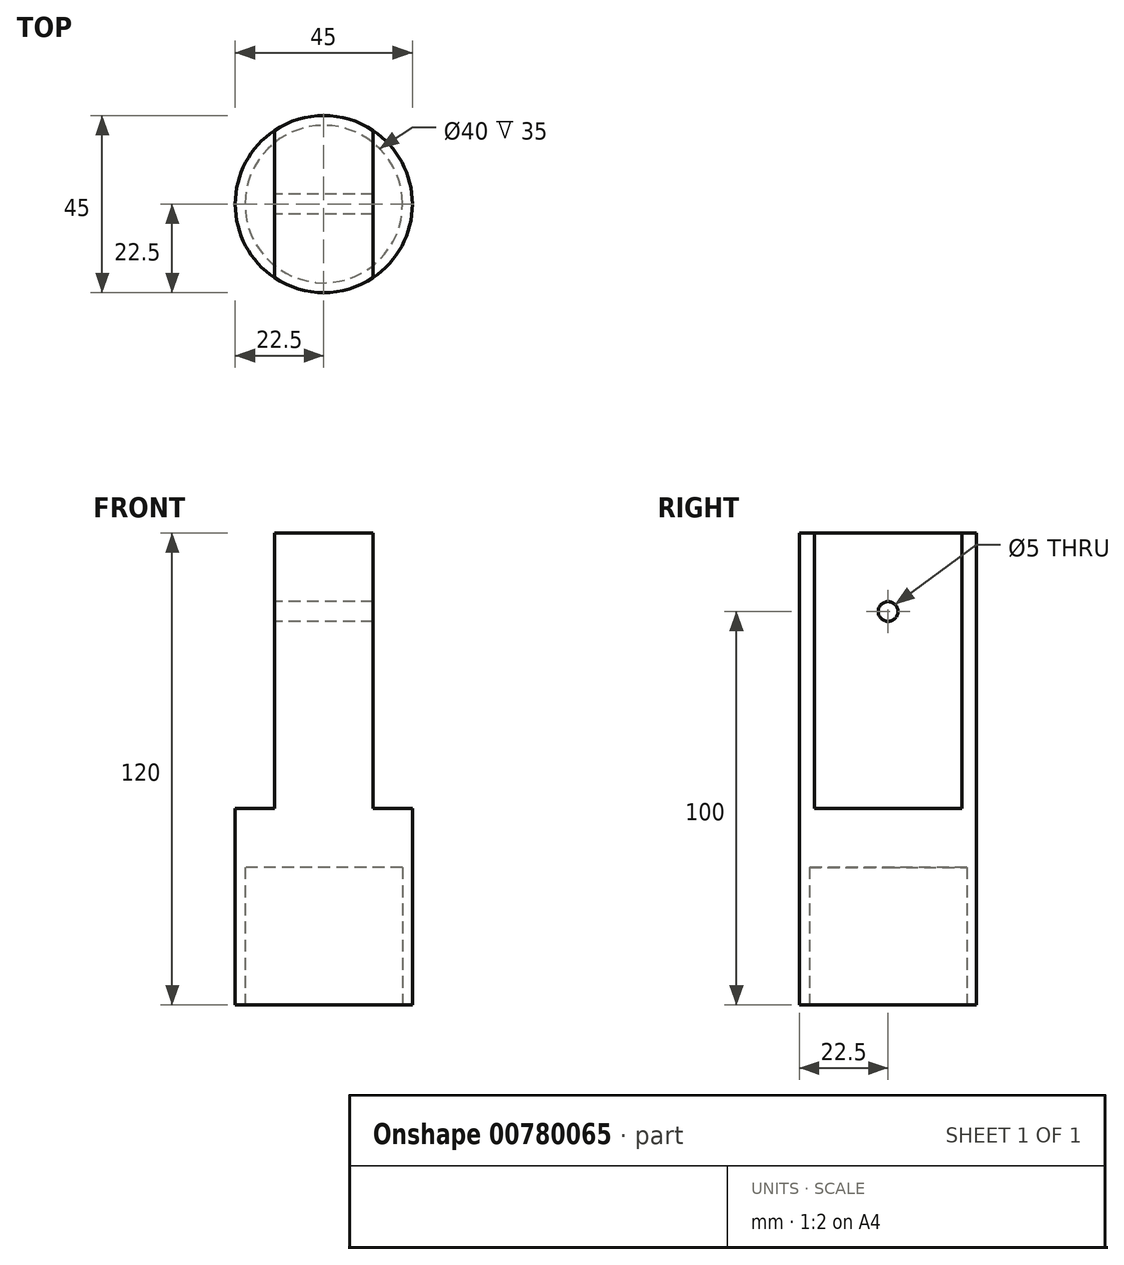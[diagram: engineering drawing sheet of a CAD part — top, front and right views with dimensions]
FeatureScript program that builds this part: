
annotation { "Feature Type Name" : "Feature", "Feature Type Description" : "" }
export const myFeature = defineFeature(function(context is Context, id is Id, definition is map)
    precondition{}
    {
        {
            var Q0;
            Q0=qCreatedBy(makeId("Top.planeOp"),FACE);
            var sketch = newSketch(context, id + "F0", { "sketchPlane" : qUnion([Q0])});
            skCircle(sketch, "E0", {"center": v(0, 0) * mm, "radius": 22.5 * mm});
            skSolve(sketch);
        }
        {
            var Q0;
            Q0=qSketchRegion(id+"F0",true);
            extrude(context, id + "F1", {"entities" : qUnion([Q0]), "depth" : 120 * mm, "offsetDistance" : 25 * mm});
        }
        {
            var Q0;
            Q0=makeQuery(id+"F1.opExtrude","CAP_FACE",FACE,{"disambiguationData":[OSD([sQuery(id+"F0.wireOp",EDGE,"E0")])],"isStart":false});
            var sketch = newSketch(context, id + "F2", { "sketchPlane" : qUnion([Q0])});
            skLineSegment(sketch, "E1", {"start": v(-12.5, 18.7) * mm, "end": v(-12.5, -18.7) * mm});
            skLineSegment(sketch, "E2", {"start": v(12.5, 18.7) * mm, "end": v(12.5, -18.7) * mm});
            skSolve(sketch);
        }
        {
            var Q0;
            {var subQ0=sQuery(id+"F2.wireOp",EDGE,"E2");Q0=makeQuery(id+"F2.imprint","IMPRINT",FACE,{"disambiguationData":[TD([[makeQuery(id+"F2.imprint","IMPRINT",EDGE,{"derivedFrom":subQ0}),1.0]])]});}
            var Q1;
            {var subQ0=sQuery(id+"F2.wireOp",EDGE,"E1");Q1=makeQuery(id+"F2.imprint","IMPRINT",FACE,{"disambiguationData":[TD([[makeQuery(id+"F2.imprint","IMPRINT",EDGE,{"derivedFrom":subQ0}),-1.0]])]});}
            extrude(context, id + "F3", {"entities" : qUnion([Q0, Q1]), "operationType" : NewBodyOperationType.REMOVE, "oppositeDirection" : true, "depth" : 70 * mm, "offsetDistance" : 25 * mm});
        }
        {
            var Q0;
            Q0=qCreatedBy(makeId("Top.planeOp"),FACE);
            var sketch = newSketch(context, id + "F4", { "sketchPlane" : qUnion([Q0])});
            skCircle(sketch, "E3", {"center": v(0, 0) * mm, "radius": 20 * mm});
            skSolve(sketch);
        }
        {
            var Q0;
            Q0=qSketchRegion(id+"F4",true);
            extrude(context, id + "F5", {"entities" : qUnion([Q0]), "operationType" : NewBodyOperationType.REMOVE, "depth" : 35 * mm, "offsetDistance" : 25 * mm});
        }
        {
            var Q0;
            Q0=qCreatedBy(makeId("Right.planeOp"),FACE);
            var sketch = newSketch(context, id + "F6", { "sketchPlane" : qUnion([Q0])});
            skCircle(sketch, "E4", {"center": v(0, 100) * mm, "radius": 2.5 * mm});
            skSolve(sketch);
        }
        {
            var Q0;
            Q0=qSketchRegion(id+"F6",true);
            extrude(context, id + "F7", {"entities" : qUnion([Q0]), "operationType" : NewBodyOperationType.REMOVE, "endBound" : BoundingType.SYMMETRIC, "depth" : 100 * mm, "offsetDistance" : 25 * mm});
        }
    });
